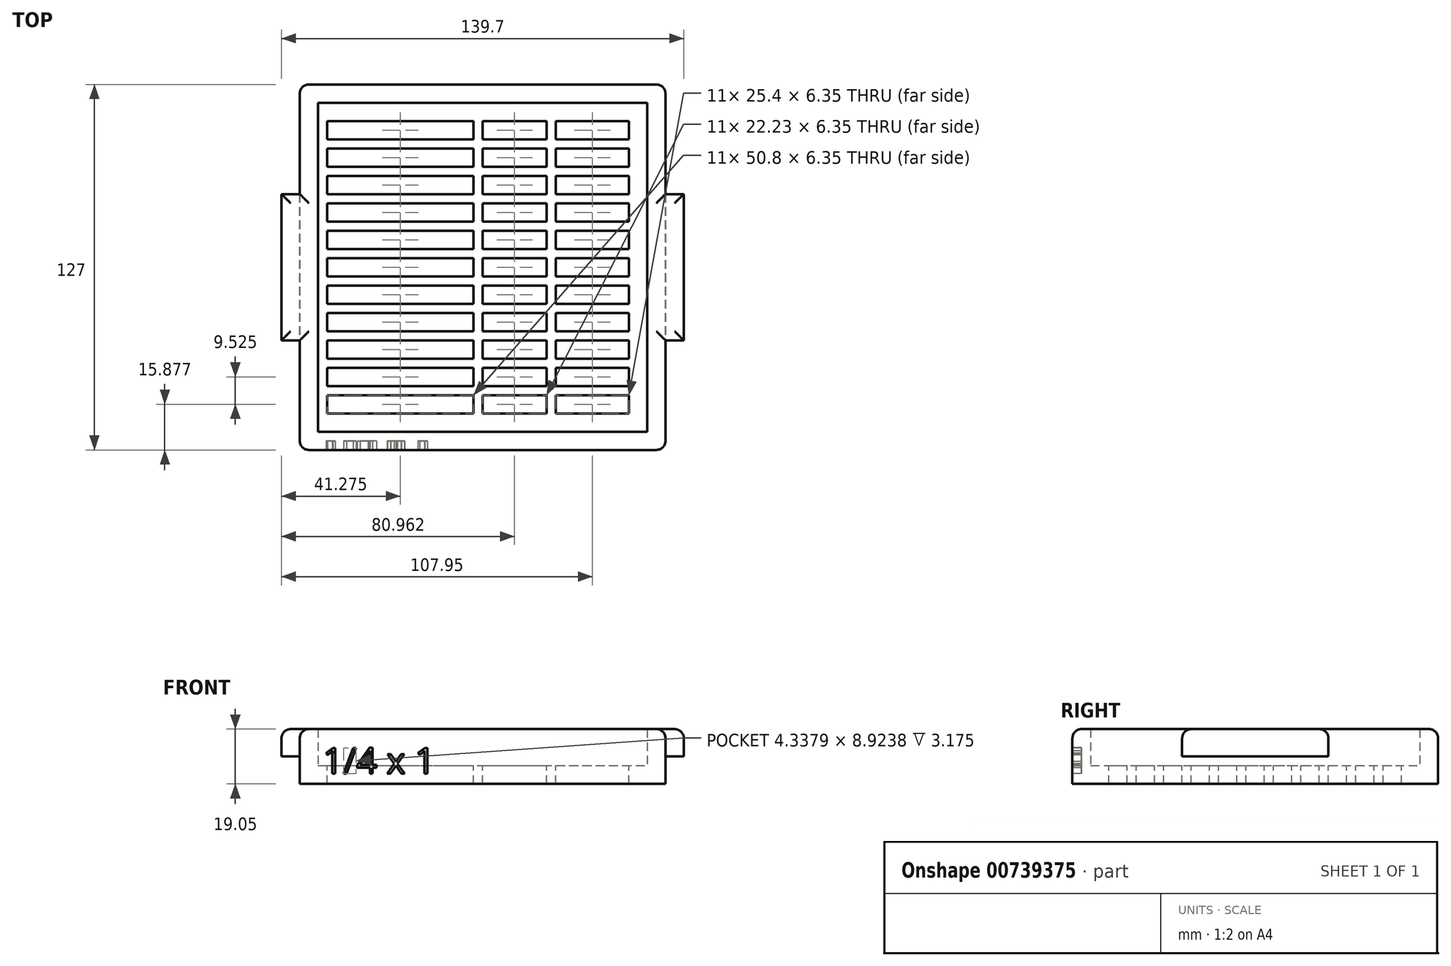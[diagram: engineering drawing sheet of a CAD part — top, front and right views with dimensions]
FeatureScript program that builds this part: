
annotation { "Feature Type Name" : "Feature", "Feature Type Description" : "" }
export const myFeature = defineFeature(function(context is Context, id is Id, definition is map)
    precondition{}
    {
        {
            var Q0;
            Q0=qCreatedBy(makeId("Top.planeOp"),FACE);
            var sketch = newSketch(context, id + "F0", { "sketchPlane" : qUnion([Q0])});
            skLineSegment(sketch, "E0.bottom", {"start": v(-63.5, -63.76) * mm, "end": v(63.5, -63.76) * mm});
            skLineSegment(sketch, "E0.top", {"start": v(-63.5, 63.24) * mm, "end": v(63.5, 63.24) * mm});
            skLineSegment(sketch, "E0.left", {"start": v(-63.5, -63.76) * mm, "end": v(-63.5, 63.24) * mm});
            skLineSegment(sketch, "E0.right", {"start": v(63.5, -63.76) * mm, "end": v(63.5, 63.24) * mm});
            skLineSegment(sketch, "E1.bottom", {"start": v(-57.15, -57.4) * mm, "end": v(57.15, -57.4) * mm});
            skLineSegment(sketch, "E1.top", {"start": v(-57.15, 56.9) * mm, "end": v(57.15, 56.9) * mm});
            skLineSegment(sketch, "E1.left", {"start": v(-57.15, -57.4) * mm, "end": v(-57.15, 56.9) * mm});
            skLineSegment(sketch, "E1.right", {"start": v(57.15, -57.4) * mm, "end": v(57.15, 56.9) * mm});
            skPoint(sketch, "E2", {"position": v(-63.5, -0.26) * mm});
            skPoint(sketch, "E3", {"position": v(63.5, -0.26) * mm});
            skLineSegment(sketch, "E4.bottom", {"start": v(-69.85, 25.14) * mm, "end": v(-57.15, 25.14) * mm});
            skLineSegment(sketch, "E4.top", {"start": v(-69.85, -25.66) * mm, "end": v(-57.15, -25.66) * mm});
            skLineSegment(sketch, "E4.left", {"start": v(-69.85, 25.14) * mm, "end": v(-69.85, -25.66) * mm});
            skLineSegment(sketch, "E4.right", {"start": v(-57.15, 25.14) * mm, "end": v(-57.15, -25.66) * mm});
            skLineSegment(sketch, "E5.bottom", {"start": v(69.85, 25.14) * mm, "end": v(57.15, 25.14) * mm});
            skLineSegment(sketch, "E5.top", {"start": v(69.85, -25.66) * mm, "end": v(57.15, -25.66) * mm});
            skLineSegment(sketch, "E5.left", {"start": v(69.85, 25.14) * mm, "end": v(69.85, -25.66) * mm});
            skLineSegment(sketch, "E5.right", {"start": v(57.15, 25.14) * mm, "end": v(57.15, -25.66) * mm});
            skPoint(sketch, "E5.cornerSnap0", {"position": v(-63.5, 25.14) * mm});
            skSolve(sketch);
        }
        {
            var Q0;
            {var subQ3=sQuery(id+"F0.wireOp",EDGE,"E1.bottom");Q0=makeQuery(id+"F0.imprint","IMPRINT",FACE,{"disambiguationData":[TD([[makeQuery(id+"F0.imprint","IMPRINT",EDGE,{"derivedFrom":subQ3}),1.0]])]});}
            extrude(context, id + "F1", {"entities" : qUnion([Q0]), "depth" : 6.35 * mm, "offsetDistance" : 25.4 * mm});
        }
        {
            var Q0;
            Q0=qSketchRegion(id+"F0",true);
            extrude(context, id + "F2", {"entities" : qUnion([Q0]), "operationType" : NewBodyOperationType.ADD, "depth" : 19.05 * mm, "offsetDistance" : 25.4 * mm});
        }
        {
            var Q0;
            Q0=makeQuery(id+"F1.opExtrude","CAP_FACE",FACE,{"disambiguationData":[OSD([sQuery(id+"F0.wireOp",EDGE,"E1.bottom"),sQuery(id+"F0.wireOp",EDGE,"E1.top"),sQuery(id+"F0.wireOp",EDGE,"E1.left"),sQuery(id+"F0.wireOp",EDGE,"E1.right"),sQuery(id+"F0.wireOp",EDGE,"E4.right"),sQuery(id+"F0.wireOp",EDGE,"E5.right")])],"isStart":false});
            var sketch = newSketch(context, id + "F3", { "sketchPlane" : qUnion([Q0])});
            skLineSegment(sketch, "E6.bottom", {"start": v(-53.97, -51.06) * mm, "end": v(-25.4, -51.06) * mm});
            skLineSegment(sketch, "E6.top", {"start": v(-53.98, -44.7) * mm, "end": v(-25.4, -44.7) * mm});
            skLineSegment(sketch, "E6.left", {"start": v(-53.97, -51.06) * mm, "end": v(-53.97, -44.7) * mm});
            skLineSegment(sketch, "E6.right", {"start": v(-25.4, -51.06) * mm, "end": v(-25.4, -44.7) * mm});
            skLineSegment(sketch, "E7.0.1.0", {"start": v(-53.97, -41.53) * mm, "end": v(-25.4, -41.53) * mm});
            skLineSegment(sketch, "E7.0.1.1", {"start": v(-53.98, -35.18) * mm, "end": v(-25.4, -35.18) * mm});
            skLineSegment(sketch, "E7.0.1.2", {"start": v(-53.97, -41.53) * mm, "end": v(-53.97, -35.18) * mm});
            skLineSegment(sketch, "E7.0.1.3", {"start": v(-25.4, -41.53) * mm, "end": v(-25.4, -35.18) * mm});
            skLineSegment(sketch, "E7.0.2.0", {"start": v(-53.97, -32) * mm, "end": v(-25.4, -32) * mm});
            skLineSegment(sketch, "E7.0.2.1", {"start": v(-53.98, -25.66) * mm, "end": v(-25.4, -25.66) * mm});
            skLineSegment(sketch, "E7.0.2.2", {"start": v(-53.97, -32) * mm, "end": v(-53.97, -25.66) * mm});
            skLineSegment(sketch, "E7.0.2.3", {"start": v(-25.4, -32) * mm, "end": v(-25.4, -25.66) * mm});
            skLineSegment(sketch, "E7.0.3.0", {"start": v(-53.97, -22.48) * mm, "end": v(-25.4, -22.48) * mm});
            skLineSegment(sketch, "E7.0.3.1", {"start": v(-53.98, -16.13) * mm, "end": v(-25.4, -16.13) * mm});
            skLineSegment(sketch, "E7.0.3.2", {"start": v(-53.97, -22.48) * mm, "end": v(-53.97, -16.13) * mm});
            skLineSegment(sketch, "E7.0.3.3", {"start": v(-25.4, -22.48) * mm, "end": v(-25.4, -16.13) * mm});
            skLineSegment(sketch, "E7.0.4.0", {"start": v(-53.97, -12.96) * mm, "end": v(-25.4, -12.96) * mm});
            skLineSegment(sketch, "E7.0.4.1", {"start": v(-53.98, -6.6) * mm, "end": v(-25.4, -6.6) * mm});
            skLineSegment(sketch, "E7.0.4.2", {"start": v(-53.97, -12.96) * mm, "end": v(-53.97, -6.6) * mm});
            skLineSegment(sketch, "E7.0.4.3", {"start": v(-25.4, -12.96) * mm, "end": v(-25.4, -6.6) * mm});
            skLineSegment(sketch, "E7.0.5.0", {"start": v(-53.97, -3.43) * mm, "end": v(-25.4, -3.43) * mm});
            skLineSegment(sketch, "E7.0.5.1", {"start": v(-53.98, 2.92) * mm, "end": v(-25.4, 2.92) * mm});
            skLineSegment(sketch, "E7.0.5.2", {"start": v(-53.97, -3.43) * mm, "end": v(-53.97, 2.92) * mm});
            skLineSegment(sketch, "E7.0.5.3", {"start": v(-25.4, -3.43) * mm, "end": v(-25.4, 2.92) * mm});
            skLineSegment(sketch, "E7.0.6.0", {"start": v(-53.97, 6.1) * mm, "end": v(-25.4, 6.1) * mm});
            skLineSegment(sketch, "E7.0.6.1", {"start": v(-53.98, 12.44) * mm, "end": v(-25.4, 12.44) * mm});
            skLineSegment(sketch, "E7.0.6.2", {"start": v(-53.97, 6.1) * mm, "end": v(-53.97, 12.44) * mm});
            skLineSegment(sketch, "E7.0.6.3", {"start": v(-25.4, 6.1) * mm, "end": v(-25.4, 12.44) * mm});
            skLineSegment(sketch, "E7.0.7.0", {"start": v(-53.97, 15.62) * mm, "end": v(-25.4, 15.62) * mm});
            skLineSegment(sketch, "E7.0.7.1", {"start": v(-53.98, 21.97) * mm, "end": v(-25.4, 21.97) * mm});
            skLineSegment(sketch, "E7.0.7.2", {"start": v(-53.97, 15.62) * mm, "end": v(-53.97, 21.97) * mm});
            skLineSegment(sketch, "E7.0.7.3", {"start": v(-25.4, 15.62) * mm, "end": v(-25.4, 21.97) * mm});
            skLineSegment(sketch, "E7.0.8.0", {"start": v(-53.97, 25.14) * mm, "end": v(-25.4, 25.14) * mm});
            skLineSegment(sketch, "E7.0.8.1", {"start": v(-53.98, 31.5) * mm, "end": v(-25.4, 31.5) * mm});
            skLineSegment(sketch, "E7.0.8.2", {"start": v(-53.97, 25.14) * mm, "end": v(-53.97, 31.5) * mm});
            skLineSegment(sketch, "E7.0.8.3", {"start": v(-25.4, 25.14) * mm, "end": v(-25.4, 31.5) * mm});
            skLineSegment(sketch, "E7.0.9.0", {"start": v(-53.97, 34.67) * mm, "end": v(-25.4, 34.67) * mm});
            skLineSegment(sketch, "E7.0.9.1", {"start": v(-53.98, 41.02) * mm, "end": v(-25.4, 41.02) * mm});
            skLineSegment(sketch, "E7.0.9.2", {"start": v(-53.97, 34.67) * mm, "end": v(-53.97, 41.02) * mm});
            skLineSegment(sketch, "E7.0.9.3", {"start": v(-25.4, 34.67) * mm, "end": v(-25.4, 41.02) * mm});
            skLineSegment(sketch, "E7.0.10.0", {"start": v(-53.97, 44.2) * mm, "end": v(-25.4, 44.2) * mm});
            skLineSegment(sketch, "E7.0.10.1", {"start": v(-53.98, 50.54) * mm, "end": v(-25.4, 50.54) * mm});
            skLineSegment(sketch, "E7.0.10.2", {"start": v(-53.97, 44.2) * mm, "end": v(-53.97, 50.54) * mm});
            skLineSegment(sketch, "E7.0.10.3", {"start": v(-25.4, 44.2) * mm, "end": v(-25.4, 50.54) * mm});
            skLineSegment(sketch, "E7.1.0.0", {"start": v(-28.57, -51.06) * mm, "end": v(0, -51.06) * mm});
            skLineSegment(sketch, "E7.1.0.1", {"start": v(-28.58, -44.7) * mm, "end": v(0, -44.7) * mm});
            skLineSegment(sketch, "E7.1.0.2", {"start": v(-28.57, -51.06) * mm, "end": v(-28.57, -44.7) * mm});
            skLineSegment(sketch, "E7.1.0.3", {"start": v(0, -51.06) * mm, "end": v(0, -44.7) * mm});
            skLineSegment(sketch, "E7.1.1.0", {"start": v(-28.57, -41.53) * mm, "end": v(0, -41.53) * mm});
            skLineSegment(sketch, "E7.1.1.1", {"start": v(-28.58, -35.18) * mm, "end": v(0, -35.18) * mm});
            skLineSegment(sketch, "E7.1.1.2", {"start": v(-28.57, -41.53) * mm, "end": v(-28.58, -35.18) * mm});
            skLineSegment(sketch, "E7.1.1.3", {"start": v(0, -41.53) * mm, "end": v(0, -35.18) * mm});
            skLineSegment(sketch, "E7.1.2.0", {"start": v(-28.57, -32) * mm, "end": v(0, -32) * mm});
            skLineSegment(sketch, "E7.1.2.1", {"start": v(-28.58, -25.66) * mm, "end": v(0, -25.66) * mm});
            skLineSegment(sketch, "E7.1.2.2", {"start": v(-28.57, -32) * mm, "end": v(-28.58, -25.66) * mm});
            skLineSegment(sketch, "E7.1.2.3", {"start": v(0, -32) * mm, "end": v(0, -25.66) * mm});
            skLineSegment(sketch, "E7.1.3.0", {"start": v(-28.57, -22.48) * mm, "end": v(0, -22.48) * mm});
            skLineSegment(sketch, "E7.1.3.1", {"start": v(-28.58, -16.13) * mm, "end": v(0, -16.13) * mm});
            skLineSegment(sketch, "E7.1.3.2", {"start": v(-28.58, -22.48) * mm, "end": v(-28.58, -16.13) * mm});
            skLineSegment(sketch, "E7.1.3.3", {"start": v(0, -22.48) * mm, "end": v(0, -16.13) * mm});
            skLineSegment(sketch, "E7.1.4.0", {"start": v(-28.57, -12.96) * mm, "end": v(0, -12.96) * mm});
            skLineSegment(sketch, "E7.1.4.1", {"start": v(-28.58, -6.6) * mm, "end": v(0, -6.6) * mm});
            skLineSegment(sketch, "E7.1.4.2", {"start": v(-28.58, -12.96) * mm, "end": v(-28.58, -6.6) * mm});
            skLineSegment(sketch, "E7.1.4.3", {"start": v(0, -12.96) * mm, "end": v(0, -6.6) * mm});
            skLineSegment(sketch, "E7.1.5.0", {"start": v(-28.57, -3.43) * mm, "end": v(0, -3.43) * mm});
            skLineSegment(sketch, "E7.1.5.1", {"start": v(-28.58, 2.92) * mm, "end": v(0, 2.92) * mm});
            skLineSegment(sketch, "E7.1.5.2", {"start": v(-28.58, -3.43) * mm, "end": v(-28.58, 2.92) * mm});
            skLineSegment(sketch, "E7.1.5.3", {"start": v(0, -3.43) * mm, "end": v(0, 2.92) * mm});
            skLineSegment(sketch, "E7.1.6.0", {"start": v(-28.57, 6.1) * mm, "end": v(0, 6.1) * mm});
            skLineSegment(sketch, "E7.1.6.1", {"start": v(-28.58, 12.44) * mm, "end": v(0, 12.44) * mm});
            skLineSegment(sketch, "E7.1.6.2", {"start": v(-28.58, 6.1) * mm, "end": v(-28.58, 12.44) * mm});
            skLineSegment(sketch, "E7.1.6.3", {"start": v(0, 6.1) * mm, "end": v(0, 12.44) * mm});
            skLineSegment(sketch, "E7.1.7.0", {"start": v(-28.57, 15.62) * mm, "end": v(0, 15.62) * mm});
            skLineSegment(sketch, "E7.1.7.1", {"start": v(-28.58, 21.97) * mm, "end": v(0, 21.97) * mm});
            skLineSegment(sketch, "E7.1.7.2", {"start": v(-28.58, 15.62) * mm, "end": v(-28.58, 21.97) * mm});
            skLineSegment(sketch, "E7.1.7.3", {"start": v(0, 15.62) * mm, "end": v(0, 21.97) * mm});
            skLineSegment(sketch, "E7.1.8.0", {"start": v(-28.57, 25.14) * mm, "end": v(0, 25.14) * mm});
            skLineSegment(sketch, "E7.1.8.1", {"start": v(-28.58, 31.5) * mm, "end": v(0, 31.5) * mm});
            skLineSegment(sketch, "E7.1.8.2", {"start": v(-28.58, 25.14) * mm, "end": v(-28.58, 31.5) * mm});
            skLineSegment(sketch, "E7.1.8.3", {"start": v(0, 25.14) * mm, "end": v(0, 31.5) * mm});
            skLineSegment(sketch, "E7.1.9.0", {"start": v(-28.57, 34.67) * mm, "end": v(0, 34.67) * mm});
            skLineSegment(sketch, "E7.1.9.1", {"start": v(-28.58, 41.02) * mm, "end": v(0, 41.02) * mm});
            skLineSegment(sketch, "E7.1.9.2", {"start": v(-28.58, 34.67) * mm, "end": v(-28.58, 41.02) * mm});
            skLineSegment(sketch, "E7.1.9.3", {"start": v(0, 34.67) * mm, "end": v(0, 41.02) * mm});
            skLineSegment(sketch, "E7.1.10.0", {"start": v(-28.57, 44.2) * mm, "end": v(0, 44.2) * mm});
            skLineSegment(sketch, "E7.1.10.1", {"start": v(-28.58, 50.54) * mm, "end": v(0, 50.54) * mm});
            skLineSegment(sketch, "E7.1.10.2", {"start": v(-28.58, 44.2) * mm, "end": v(-28.58, 50.54) * mm});
            skLineSegment(sketch, "E7.1.10.3", {"start": v(0, 44.2) * mm, "end": v(0, 50.54) * mm});
            skLineSegment(sketch, "E7.2.0.0", {"start": v(-3.18, -51.06) * mm, "end": v(25.4, -51.06) * mm});
            skLineSegment(sketch, "E7.2.0.1", {"start": v(-3.18, -44.7) * mm, "end": v(25.4, -44.7) * mm});
            skLineSegment(sketch, "E7.2.0.2", {"start": v(-3.18, -51.06) * mm, "end": v(-3.18, -44.7) * mm});
            skLineSegment(sketch, "E7.2.0.3", {"start": v(25.4, -51.06) * mm, "end": v(25.4, -44.7) * mm});
            skLineSegment(sketch, "E7.2.1.0", {"start": v(-3.18, -41.53) * mm, "end": v(25.4, -41.53) * mm});
            skLineSegment(sketch, "E7.2.1.1", {"start": v(-3.18, -35.18) * mm, "end": v(25.4, -35.18) * mm});
            skLineSegment(sketch, "E7.2.1.2", {"start": v(-3.18, -41.53) * mm, "end": v(-3.18, -35.18) * mm});
            skLineSegment(sketch, "E7.2.1.3", {"start": v(25.4, -41.53) * mm, "end": v(25.4, -35.18) * mm});
            skLineSegment(sketch, "E7.2.2.0", {"start": v(-3.18, -32) * mm, "end": v(25.4, -32) * mm});
            skLineSegment(sketch, "E7.2.2.1", {"start": v(-3.18, -25.66) * mm, "end": v(25.4, -25.66) * mm});
            skLineSegment(sketch, "E7.2.2.2", {"start": v(-3.18, -32) * mm, "end": v(-3.18, -25.66) * mm});
            skLineSegment(sketch, "E7.2.2.3", {"start": v(25.4, -32) * mm, "end": v(25.4, -25.66) * mm});
            skLineSegment(sketch, "E7.2.3.0", {"start": v(-3.18, -22.48) * mm, "end": v(25.4, -22.48) * mm});
            skLineSegment(sketch, "E7.2.3.1", {"start": v(-3.18, -16.13) * mm, "end": v(25.4, -16.13) * mm});
            skLineSegment(sketch, "E7.2.3.2", {"start": v(-3.18, -22.48) * mm, "end": v(-3.18, -16.13) * mm});
            skLineSegment(sketch, "E7.2.3.3", {"start": v(25.4, -22.48) * mm, "end": v(25.4, -16.13) * mm});
            skLineSegment(sketch, "E7.2.4.0", {"start": v(-3.18, -12.96) * mm, "end": v(25.4, -12.96) * mm});
            skLineSegment(sketch, "E7.2.4.1", {"start": v(-3.18, -6.6) * mm, "end": v(25.4, -6.6) * mm});
            skLineSegment(sketch, "E7.2.4.2", {"start": v(-3.18, -12.96) * mm, "end": v(-3.18, -6.6) * mm});
            skLineSegment(sketch, "E7.2.4.3", {"start": v(25.4, -12.96) * mm, "end": v(25.4, -6.6) * mm});
            skLineSegment(sketch, "E7.2.5.0", {"start": v(-3.18, -3.43) * mm, "end": v(25.4, -3.43) * mm});
            skLineSegment(sketch, "E7.2.5.1", {"start": v(-3.18, 2.92) * mm, "end": v(25.4, 2.92) * mm});
            skLineSegment(sketch, "E7.2.5.2", {"start": v(-3.18, -3.43) * mm, "end": v(-3.18, 2.92) * mm});
            skLineSegment(sketch, "E7.2.5.3", {"start": v(25.4, -3.43) * mm, "end": v(25.4, 2.92) * mm});
            skLineSegment(sketch, "E7.2.6.0", {"start": v(-3.18, 6.1) * mm, "end": v(25.4, 6.1) * mm});
            skLineSegment(sketch, "E7.2.6.1", {"start": v(-3.18, 12.44) * mm, "end": v(25.4, 12.44) * mm});
            skLineSegment(sketch, "E7.2.6.2", {"start": v(-3.18, 6.1) * mm, "end": v(-3.18, 12.44) * mm});
            skLineSegment(sketch, "E7.2.6.3", {"start": v(25.4, 6.1) * mm, "end": v(25.4, 12.44) * mm});
            skLineSegment(sketch, "E7.2.7.0", {"start": v(-3.18, 15.62) * mm, "end": v(25.4, 15.62) * mm});
            skLineSegment(sketch, "E7.2.7.1", {"start": v(-3.18, 21.97) * mm, "end": v(25.4, 21.97) * mm});
            skLineSegment(sketch, "E7.2.7.2", {"start": v(-3.18, 15.62) * mm, "end": v(-3.18, 21.97) * mm});
            skLineSegment(sketch, "E7.2.7.3", {"start": v(25.4, 15.62) * mm, "end": v(25.4, 21.97) * mm});
            skLineSegment(sketch, "E7.2.8.0", {"start": v(-3.18, 25.14) * mm, "end": v(25.4, 25.14) * mm});
            skLineSegment(sketch, "E7.2.8.1", {"start": v(-3.18, 31.5) * mm, "end": v(25.4, 31.5) * mm});
            skLineSegment(sketch, "E7.2.8.2", {"start": v(-3.18, 25.14) * mm, "end": v(-3.18, 31.5) * mm});
            skLineSegment(sketch, "E7.2.8.3", {"start": v(25.4, 25.14) * mm, "end": v(25.4, 31.5) * mm});
            skLineSegment(sketch, "E7.2.9.0", {"start": v(-3.18, 34.67) * mm, "end": v(25.4, 34.67) * mm});
            skLineSegment(sketch, "E7.2.9.1", {"start": v(-3.18, 41.02) * mm, "end": v(25.4, 41.02) * mm});
            skLineSegment(sketch, "E7.2.9.2", {"start": v(-3.18, 34.67) * mm, "end": v(-3.18, 41.02) * mm});
            skLineSegment(sketch, "E7.2.9.3", {"start": v(25.4, 34.67) * mm, "end": v(25.4, 41.02) * mm});
            skLineSegment(sketch, "E7.2.10.0", {"start": v(-3.18, 44.2) * mm, "end": v(25.4, 44.2) * mm});
            skLineSegment(sketch, "E7.2.10.1", {"start": v(-3.18, 50.54) * mm, "end": v(25.4, 50.54) * mm});
            skLineSegment(sketch, "E7.2.10.2", {"start": v(-3.18, 44.2) * mm, "end": v(-3.18, 50.54) * mm});
            skLineSegment(sketch, "E7.2.10.3", {"start": v(25.4, 44.2) * mm, "end": v(25.4, 50.54) * mm});
            skLineSegment(sketch, "E7.3.0.0", {"start": v(22.22, -51.06) * mm, "end": v(50.8, -51.06) * mm});
            skLineSegment(sketch, "E7.3.0.1", {"start": v(22.22, -44.7) * mm, "end": v(50.8, -44.7) * mm});
            skLineSegment(sketch, "E7.3.0.2", {"start": v(22.22, -51.06) * mm, "end": v(22.22, -44.7) * mm});
            skLineSegment(sketch, "E7.3.0.3", {"start": v(50.8, -51.06) * mm, "end": v(50.8, -44.7) * mm});
            skLineSegment(sketch, "E7.3.1.0", {"start": v(22.22, -41.53) * mm, "end": v(50.8, -41.53) * mm});
            skLineSegment(sketch, "E7.3.1.1", {"start": v(22.22, -35.18) * mm, "end": v(50.8, -35.18) * mm});
            skLineSegment(sketch, "E7.3.1.2", {"start": v(22.22, -41.53) * mm, "end": v(22.22, -35.18) * mm});
            skLineSegment(sketch, "E7.3.1.3", {"start": v(50.8, -41.53) * mm, "end": v(50.8, -35.18) * mm});
            skLineSegment(sketch, "E7.3.2.0", {"start": v(22.22, -32) * mm, "end": v(50.8, -32) * mm});
            skLineSegment(sketch, "E7.3.2.1", {"start": v(22.22, -25.66) * mm, "end": v(50.8, -25.66) * mm});
            skLineSegment(sketch, "E7.3.2.2", {"start": v(22.22, -32) * mm, "end": v(22.22, -25.66) * mm});
            skLineSegment(sketch, "E7.3.2.3", {"start": v(50.8, -32) * mm, "end": v(50.8, -25.66) * mm});
            skLineSegment(sketch, "E7.3.3.0", {"start": v(22.22, -22.48) * mm, "end": v(50.8, -22.48) * mm});
            skLineSegment(sketch, "E7.3.3.1", {"start": v(22.22, -16.13) * mm, "end": v(50.8, -16.13) * mm});
            skLineSegment(sketch, "E7.3.3.2", {"start": v(22.22, -22.48) * mm, "end": v(22.22, -16.13) * mm});
            skLineSegment(sketch, "E7.3.3.3", {"start": v(50.8, -22.48) * mm, "end": v(50.8, -16.13) * mm});
            skLineSegment(sketch, "E7.3.4.0", {"start": v(22.22, -12.96) * mm, "end": v(50.8, -12.96) * mm});
            skLineSegment(sketch, "E7.3.4.1", {"start": v(22.22, -6.6) * mm, "end": v(50.8, -6.6) * mm});
            skLineSegment(sketch, "E7.3.4.2", {"start": v(22.22, -12.96) * mm, "end": v(22.22, -6.6) * mm});
            skLineSegment(sketch, "E7.3.4.3", {"start": v(50.8, -12.96) * mm, "end": v(50.8, -6.6) * mm});
            skLineSegment(sketch, "E7.3.5.0", {"start": v(22.22, -3.43) * mm, "end": v(50.8, -3.43) * mm});
            skLineSegment(sketch, "E7.3.5.1", {"start": v(22.22, 2.92) * mm, "end": v(50.8, 2.92) * mm});
            skLineSegment(sketch, "E7.3.5.2", {"start": v(22.22, -3.43) * mm, "end": v(22.22, 2.92) * mm});
            skLineSegment(sketch, "E7.3.5.3", {"start": v(50.8, -3.43) * mm, "end": v(50.8, 2.92) * mm});
            skLineSegment(sketch, "E7.3.6.0", {"start": v(22.22, 6.1) * mm, "end": v(50.8, 6.1) * mm});
            skLineSegment(sketch, "E7.3.6.1", {"start": v(22.22, 12.44) * mm, "end": v(50.8, 12.44) * mm});
            skLineSegment(sketch, "E7.3.6.2", {"start": v(22.22, 6.1) * mm, "end": v(22.22, 12.44) * mm});
            skLineSegment(sketch, "E7.3.6.3", {"start": v(50.8, 6.1) * mm, "end": v(50.8, 12.44) * mm});
            skLineSegment(sketch, "E7.3.7.0", {"start": v(22.22, 15.62) * mm, "end": v(50.8, 15.62) * mm});
            skLineSegment(sketch, "E7.3.7.1", {"start": v(22.22, 21.97) * mm, "end": v(50.8, 21.97) * mm});
            skLineSegment(sketch, "E7.3.7.2", {"start": v(22.22, 15.62) * mm, "end": v(22.22, 21.97) * mm});
            skLineSegment(sketch, "E7.3.7.3", {"start": v(50.8, 15.62) * mm, "end": v(50.8, 21.97) * mm});
            skLineSegment(sketch, "E7.3.8.0", {"start": v(22.22, 25.14) * mm, "end": v(50.8, 25.14) * mm});
            skLineSegment(sketch, "E7.3.8.1", {"start": v(22.22, 31.5) * mm, "end": v(50.8, 31.5) * mm});
            skLineSegment(sketch, "E7.3.8.2", {"start": v(22.22, 25.14) * mm, "end": v(22.22, 31.5) * mm});
            skLineSegment(sketch, "E7.3.8.3", {"start": v(50.8, 25.14) * mm, "end": v(50.8, 31.5) * mm});
            skLineSegment(sketch, "E7.3.9.0", {"start": v(22.22, 34.67) * mm, "end": v(50.8, 34.67) * mm});
            skLineSegment(sketch, "E7.3.9.1", {"start": v(22.22, 41.02) * mm, "end": v(50.8, 41.02) * mm});
            skLineSegment(sketch, "E7.3.9.2", {"start": v(22.22, 34.67) * mm, "end": v(22.22, 41.02) * mm});
            skLineSegment(sketch, "E7.3.9.3", {"start": v(50.8, 34.67) * mm, "end": v(50.8, 41.02) * mm});
            skLineSegment(sketch, "E7.3.10.0", {"start": v(22.22, 44.2) * mm, "end": v(50.8, 44.2) * mm});
            skLineSegment(sketch, "E7.3.10.1", {"start": v(22.22, 50.54) * mm, "end": v(50.8, 50.54) * mm});
            skLineSegment(sketch, "E7.3.10.2", {"start": v(22.22, 44.2) * mm, "end": v(22.22, 50.54) * mm});
            skLineSegment(sketch, "E7.3.10.3", {"start": v(50.8, 44.2) * mm, "end": v(50.8, 50.54) * mm});
            skLineSegment(sketch, "E7.direction1", {"start": v(-53.97, -51.06) * mm, "end": v(-28.57, -51.06) * mm, "construction": true});
            skLineSegment(sketch, "E7.direction2", {"start": v(-53.97, -51.06) * mm, "end": v(-53.97, -41.53) * mm, "construction": true});
            skSolve(sketch);
        }
        {
            var Q0;
            Q0=makeQuery(id+"F3.imprint","IMPRINT",FACE,{"disambiguationData":[TD([[makeQuery(id+"F3.imprint","IMPRINT",EDGE,{"derivedFrom":sQuery(id+"F3.wireOp",EDGE,"E6.bottom")}),1.0]])]});
            var Q1;
            Q1=makeQuery(id+"F3.imprint","IMPRINT",FACE,{"disambiguationData":[TD([[makeQuery(id+"F3.imprint","IMPRINT",EDGE,{"derivedFrom":sQuery(id+"F3.wireOp",EDGE,"E7.0.1.0")}),1.0]])]});
            var Q2;
            Q2=makeQuery(id+"F3.imprint","IMPRINT",FACE,{"disambiguationData":[TD([[makeQuery(id+"F3.imprint","IMPRINT",EDGE,{"derivedFrom":sQuery(id+"F3.wireOp",EDGE,"E7.0.2.0")}),1.0]])]});
            var Q3;
            Q3=makeQuery(id+"F3.imprint","IMPRINT",FACE,{"disambiguationData":[TD([[makeQuery(id+"F3.imprint","IMPRINT",EDGE,{"derivedFrom":sQuery(id+"F3.wireOp",EDGE,"E7.0.3.0")}),1.0]])]});
            var Q4;
            Q4=makeQuery(id+"F3.imprint","IMPRINT",FACE,{"disambiguationData":[TD([[makeQuery(id+"F3.imprint","IMPRINT",EDGE,{"derivedFrom":sQuery(id+"F3.wireOp",EDGE,"E7.0.4.0")}),1.0]])]});
            var Q5;
            Q5=makeQuery(id+"F3.imprint","IMPRINT",FACE,{"disambiguationData":[TD([[makeQuery(id+"F3.imprint","IMPRINT",EDGE,{"derivedFrom":sQuery(id+"F3.wireOp",EDGE,"E7.0.5.0")}),1.0]])]});
            var Q6;
            Q6=makeQuery(id+"F3.imprint","IMPRINT",FACE,{"disambiguationData":[TD([[makeQuery(id+"F3.imprint","IMPRINT",EDGE,{"derivedFrom":sQuery(id+"F3.wireOp",EDGE,"E7.0.6.0")}),1.0]])]});
            var Q7;
            Q7=makeQuery(id+"F3.imprint","IMPRINT",FACE,{"disambiguationData":[TD([[makeQuery(id+"F3.imprint","IMPRINT",EDGE,{"derivedFrom":sQuery(id+"F3.wireOp",EDGE,"E7.0.7.0")}),1.0]])]});
            var Q8;
            Q8=makeQuery(id+"F3.imprint","IMPRINT",FACE,{"disambiguationData":[TD([[makeQuery(id+"F3.imprint","IMPRINT",EDGE,{"derivedFrom":sQuery(id+"F3.wireOp",EDGE,"E7.0.8.0")}),1.0]])]});
            var Q9;
            Q9=makeQuery(id+"F3.imprint","IMPRINT",FACE,{"disambiguationData":[TD([[makeQuery(id+"F3.imprint","IMPRINT",EDGE,{"derivedFrom":sQuery(id+"F3.wireOp",EDGE,"E7.0.9.0")}),1.0]])]});
            var Q10;
            Q10=makeQuery(id+"F3.imprint","IMPRINT",FACE,{"disambiguationData":[TD([[makeQuery(id+"F3.imprint","IMPRINT",EDGE,{"derivedFrom":sQuery(id+"F3.wireOp",EDGE,"E7.0.10.0")}),1.0]])]});
            var Q11;
            Q11=makeQuery(id+"F3.imprint","IMPRINT",FACE,{"disambiguationData":[TD([[makeQuery(id+"F3.imprint","IMPRINT",EDGE,{"derivedFrom":sQuery(id+"F3.wireOp",EDGE,"E7.0.11.0")}),1.0]])]});
            var Q12;
            Q12=makeQuery(id+"F3.imprint","IMPRINT",FACE,{"disambiguationData":[TD([[makeQuery(id+"F3.imprint","IMPRINT",EDGE,{"derivedFrom":sQuery(id+"F3.wireOp",EDGE,"E7.0.12.0")}),1.0]])]});
            var Q13;
            Q13=makeQuery(id+"F3.imprint","IMPRINT",FACE,{"disambiguationData":[TD([[makeQuery(id+"F3.imprint","IMPRINT",EDGE,{"derivedFrom":sQuery(id+"F3.wireOp",EDGE,"E7.0.13.0")}),1.0]])]});
            var Q14;
            Q14=makeQuery(id+"F3.imprint","IMPRINT",FACE,{"disambiguationData":[TD([[makeQuery(id+"F3.imprint","IMPRINT",EDGE,{"derivedFrom":sQuery(id+"F3.wireOp",EDGE,"E7.0.14.0")}),1.0]])]});
            var Q15;
            Q15=makeQuery(id+"F3.imprint","IMPRINT",FACE,{"disambiguationData":[TD([[makeQuery(id+"F3.imprint","IMPRINT",EDGE,{"derivedFrom":sQuery(id+"F3.wireOp",EDGE,"E7.0.15.0")}),1.0]])]});
            var Q16;
            Q16=makeQuery(id+"F3.imprint","IMPRINT",FACE,{"disambiguationData":[TD([[makeQuery(id+"F3.imprint","IMPRINT",EDGE,{"derivedFrom":sQuery(id+"F3.wireOp",EDGE,"E7.0.16.0")}),1.0]])]});
            var Q17;
            Q17=makeQuery(id+"F3.imprint","IMPRINT",FACE,{"disambiguationData":[TD([[makeQuery(id+"F3.imprint","IMPRINT",EDGE,{"derivedFrom":sQuery(id+"F3.wireOp",EDGE,"E7.0.17.0")}),1.0]])]});
            var Q18;
            Q18=makeQuery(id+"F3.imprint","IMPRINT",FACE,{"disambiguationData":[TD([[makeQuery(id+"F3.imprint","IMPRINT",EDGE,{"derivedFrom":sQuery(id+"F3.wireOp",EDGE,"E7.0.18.0")}),1.0]])]});
            var Q19;
            Q19=makeQuery(id+"F3.imprint","IMPRINT",FACE,{"disambiguationData":[TD([[makeQuery(id+"F3.imprint","IMPRINT",EDGE,{"derivedFrom":sQuery(id+"F3.wireOp",EDGE,"E7.0.19.0")}),1.0]])]});
            var Q20;
            Q20=makeQuery(id+"F3.imprint","IMPRINT",FACE,{"disambiguationData":[TD([[makeQuery(id+"F3.imprint","IMPRINT",EDGE,{"derivedFrom":sQuery(id+"F3.wireOp",EDGE,"E7.0.20.0")}),1.0]])]});
            var Q21;
            Q21=makeQuery(id+"F3.imprint","IMPRINT",FACE,{"disambiguationData":[TD([[makeQuery(id+"F3.imprint","IMPRINT",EDGE,{"derivedFrom":sQuery(id+"F3.wireOp",EDGE,"E7.0.21.0")}),1.0]])]});
            var Q22;
            {var subQ0=sQuery(id+"F3.wireOp",EDGE,"E6.right");Q22=makeQuery(id+"F3.imprint","IMPRINT",FACE,{"disambiguationData":[TD([[makeQuery(id+"F3.imprint","IMPRINT",EDGE,{"derivedFrom":subQ0}),-1.0]])]});}
            var Q23;
            {var subQ0=sQuery(id+"F3.wireOp",EDGE,"E7.0.1.3");Q23=makeQuery(id+"F3.imprint","IMPRINT",FACE,{"disambiguationData":[TD([[makeQuery(id+"F3.imprint","IMPRINT",EDGE,{"derivedFrom":subQ0}),-1.0]])]});}
            var Q24;
            {var subQ0=sQuery(id+"F3.wireOp",EDGE,"E7.1.0.3");Q24=makeQuery(id+"F3.imprint","IMPRINT",FACE,{"disambiguationData":[TD([[makeQuery(id+"F3.imprint","IMPRINT",EDGE,{"derivedFrom":subQ0}),-1.0]])]});}
            var Q25;
            {var subQ0=sQuery(id+"F3.wireOp",EDGE,"E7.1.1.3");Q25=makeQuery(id+"F3.imprint","IMPRINT",FACE,{"disambiguationData":[TD([[makeQuery(id+"F3.imprint","IMPRINT",EDGE,{"derivedFrom":subQ0}),-1.0]])]});}
            var Q26;
            {var subQ0=sQuery(id+"F3.wireOp",EDGE,"E7.2.0.3");Q26=makeQuery(id+"F3.imprint","IMPRINT",FACE,{"disambiguationData":[TD([[makeQuery(id+"F3.imprint","IMPRINT",EDGE,{"derivedFrom":subQ0}),-1.0]])]});}
            var Q27;
            {var subQ0=sQuery(id+"F3.wireOp",EDGE,"E7.2.1.3");Q27=makeQuery(id+"F3.imprint","IMPRINT",FACE,{"disambiguationData":[TD([[makeQuery(id+"F3.imprint","IMPRINT",EDGE,{"derivedFrom":subQ0}),-1.0]])]});}
            var Q28;
            {var subQ0=sQuery(id+"F3.wireOp",EDGE,"E7.2.2.3");Q28=makeQuery(id+"F3.imprint","IMPRINT",FACE,{"disambiguationData":[TD([[makeQuery(id+"F3.imprint","IMPRINT",EDGE,{"derivedFrom":subQ0}),-1.0]])]});}
            var Q29;
            {var subQ0=sQuery(id+"F3.wireOp",EDGE,"E7.2.3.3");Q29=makeQuery(id+"F3.imprint","IMPRINT",FACE,{"disambiguationData":[TD([[makeQuery(id+"F3.imprint","IMPRINT",EDGE,{"derivedFrom":subQ0}),-1.0]])]});}
            var Q30;
            {var subQ0=sQuery(id+"F3.wireOp",EDGE,"E7.1.3.3");Q30=makeQuery(id+"F3.imprint","IMPRINT",FACE,{"disambiguationData":[TD([[makeQuery(id+"F3.imprint","IMPRINT",EDGE,{"derivedFrom":subQ0}),-1.0]])]});}
            var Q31;
            {var subQ0=sQuery(id+"F3.wireOp",EDGE,"E7.1.2.3");Q31=makeQuery(id+"F3.imprint","IMPRINT",FACE,{"disambiguationData":[TD([[makeQuery(id+"F3.imprint","IMPRINT",EDGE,{"derivedFrom":subQ0}),-1.0]])]});}
            var Q32;
            {var subQ0=sQuery(id+"F3.wireOp",EDGE,"E7.0.2.3");Q32=makeQuery(id+"F3.imprint","IMPRINT",FACE,{"disambiguationData":[TD([[makeQuery(id+"F3.imprint","IMPRINT",EDGE,{"derivedFrom":subQ0}),-1.0]])]});}
            var Q33;
            {var subQ0=sQuery(id+"F3.wireOp",EDGE,"E7.0.3.3");Q33=makeQuery(id+"F3.imprint","IMPRINT",FACE,{"disambiguationData":[TD([[makeQuery(id+"F3.imprint","IMPRINT",EDGE,{"derivedFrom":subQ0}),-1.0]])]});}
            var Q34;
            {var subQ0=sQuery(id+"F3.wireOp",EDGE,"E7.2.4.3");Q34=makeQuery(id+"F3.imprint","IMPRINT",FACE,{"disambiguationData":[TD([[makeQuery(id+"F3.imprint","IMPRINT",EDGE,{"derivedFrom":subQ0}),-1.0]])]});}
            var Q35;
            {var subQ0=sQuery(id+"F3.wireOp",EDGE,"E7.2.5.3");Q35=makeQuery(id+"F3.imprint","IMPRINT",FACE,{"disambiguationData":[TD([[makeQuery(id+"F3.imprint","IMPRINT",EDGE,{"derivedFrom":subQ0}),-1.0]])]});}
            var Q36;
            {var subQ0=sQuery(id+"F3.wireOp",EDGE,"E7.2.6.3");Q36=makeQuery(id+"F3.imprint","IMPRINT",FACE,{"disambiguationData":[TD([[makeQuery(id+"F3.imprint","IMPRINT",EDGE,{"derivedFrom":subQ0}),-1.0]])]});}
            var Q37;
            {var subQ0=sQuery(id+"F3.wireOp",EDGE,"E7.1.4.3");Q37=makeQuery(id+"F3.imprint","IMPRINT",FACE,{"disambiguationData":[TD([[makeQuery(id+"F3.imprint","IMPRINT",EDGE,{"derivedFrom":subQ0}),-1.0]])]});}
            var Q38;
            {var subQ0=sQuery(id+"F3.wireOp",EDGE,"E7.1.5.3");Q38=makeQuery(id+"F3.imprint","IMPRINT",FACE,{"disambiguationData":[TD([[makeQuery(id+"F3.imprint","IMPRINT",EDGE,{"derivedFrom":subQ0}),-1.0]])]});}
            var Q39;
            {var subQ0=sQuery(id+"F3.wireOp",EDGE,"E7.1.6.3");Q39=makeQuery(id+"F3.imprint","IMPRINT",FACE,{"disambiguationData":[TD([[makeQuery(id+"F3.imprint","IMPRINT",EDGE,{"derivedFrom":subQ0}),-1.0]])]});}
            var Q40;
            {var subQ0=sQuery(id+"F3.wireOp",EDGE,"E7.0.4.3");Q40=makeQuery(id+"F3.imprint","IMPRINT",FACE,{"disambiguationData":[TD([[makeQuery(id+"F3.imprint","IMPRINT",EDGE,{"derivedFrom":subQ0}),-1.0]])]});}
            var Q41;
            {var subQ0=sQuery(id+"F3.wireOp",EDGE,"E7.0.5.3");Q41=makeQuery(id+"F3.imprint","IMPRINT",FACE,{"disambiguationData":[TD([[makeQuery(id+"F3.imprint","IMPRINT",EDGE,{"derivedFrom":subQ0}),-1.0]])]});}
            var Q42;
            {var subQ0=sQuery(id+"F3.wireOp",EDGE,"E7.0.6.3");Q42=makeQuery(id+"F3.imprint","IMPRINT",FACE,{"disambiguationData":[TD([[makeQuery(id+"F3.imprint","IMPRINT",EDGE,{"derivedFrom":subQ0}),-1.0]])]});}
            var Q43;
            {var subQ0=sQuery(id+"F3.wireOp",EDGE,"E7.0.7.3");Q43=makeQuery(id+"F3.imprint","IMPRINT",FACE,{"disambiguationData":[TD([[makeQuery(id+"F3.imprint","IMPRINT",EDGE,{"derivedFrom":subQ0}),-1.0]])]});}
            var Q44;
            {var subQ0=sQuery(id+"F3.wireOp",EDGE,"E7.0.8.3");Q44=makeQuery(id+"F3.imprint","IMPRINT",FACE,{"disambiguationData":[TD([[makeQuery(id+"F3.imprint","IMPRINT",EDGE,{"derivedFrom":subQ0}),-1.0]])]});}
            var Q45;
            {var subQ0=sQuery(id+"F3.wireOp",EDGE,"E7.0.9.3");Q45=makeQuery(id+"F3.imprint","IMPRINT",FACE,{"disambiguationData":[TD([[makeQuery(id+"F3.imprint","IMPRINT",EDGE,{"derivedFrom":subQ0}),-1.0]])]});}
            var Q46;
            {var subQ0=sQuery(id+"F3.wireOp",EDGE,"E7.0.10.3");Q46=makeQuery(id+"F3.imprint","IMPRINT",FACE,{"disambiguationData":[TD([[makeQuery(id+"F3.imprint","IMPRINT",EDGE,{"derivedFrom":subQ0}),-1.0]])]});}
            var Q47;
            {var subQ0=sQuery(id+"F3.wireOp",EDGE,"E7.1.7.3");Q47=makeQuery(id+"F3.imprint","IMPRINT",FACE,{"disambiguationData":[TD([[makeQuery(id+"F3.imprint","IMPRINT",EDGE,{"derivedFrom":subQ0}),-1.0]])]});}
            var Q48;
            {var subQ0=sQuery(id+"F3.wireOp",EDGE,"E7.1.8.3");Q48=makeQuery(id+"F3.imprint","IMPRINT",FACE,{"disambiguationData":[TD([[makeQuery(id+"F3.imprint","IMPRINT",EDGE,{"derivedFrom":subQ0}),-1.0]])]});}
            var Q49;
            {var subQ0=sQuery(id+"F3.wireOp",EDGE,"E7.1.9.3");Q49=makeQuery(id+"F3.imprint","IMPRINT",FACE,{"disambiguationData":[TD([[makeQuery(id+"F3.imprint","IMPRINT",EDGE,{"derivedFrom":subQ0}),-1.0]])]});}
            var Q50;
            {var subQ0=sQuery(id+"F3.wireOp",EDGE,"E7.1.10.3");Q50=makeQuery(id+"F3.imprint","IMPRINT",FACE,{"disambiguationData":[TD([[makeQuery(id+"F3.imprint","IMPRINT",EDGE,{"derivedFrom":subQ0}),-1.0]])]});}
            var Q51;
            {var subQ0=sQuery(id+"F3.wireOp",EDGE,"E7.2.10.3");Q51=makeQuery(id+"F3.imprint","IMPRINT",FACE,{"disambiguationData":[TD([[makeQuery(id+"F3.imprint","IMPRINT",EDGE,{"derivedFrom":subQ0}),-1.0]])]});}
            var Q52;
            {var subQ0=sQuery(id+"F3.wireOp",EDGE,"E7.2.9.3");Q52=makeQuery(id+"F3.imprint","IMPRINT",FACE,{"disambiguationData":[TD([[makeQuery(id+"F3.imprint","IMPRINT",EDGE,{"derivedFrom":subQ0}),-1.0]])]});}
            var Q53;
            {var subQ0=sQuery(id+"F3.wireOp",EDGE,"E7.2.8.3");Q53=makeQuery(id+"F3.imprint","IMPRINT",FACE,{"disambiguationData":[TD([[makeQuery(id+"F3.imprint","IMPRINT",EDGE,{"derivedFrom":subQ0}),-1.0]])]});}
            var Q54;
            {var subQ0=sQuery(id+"F3.wireOp",EDGE,"E7.2.7.3");Q54=makeQuery(id+"F3.imprint","IMPRINT",FACE,{"disambiguationData":[TD([[makeQuery(id+"F3.imprint","IMPRINT",EDGE,{"derivedFrom":subQ0}),-1.0]])]});}
            var Q55;
            {var subQ0=sQuery(id+"F3.wireOp",EDGE,"E7.0.11.3");Q55=makeQuery(id+"F3.imprint","IMPRINT",FACE,{"disambiguationData":[TD([[makeQuery(id+"F3.imprint","IMPRINT",EDGE,{"derivedFrom":subQ0}),-1.0]])]});}
            var Q56;
            {var subQ0=sQuery(id+"F3.wireOp",EDGE,"E7.0.12.3");Q56=makeQuery(id+"F3.imprint","IMPRINT",FACE,{"disambiguationData":[TD([[makeQuery(id+"F3.imprint","IMPRINT",EDGE,{"derivedFrom":subQ0}),-1.0]])]});}
            var Q57;
            {var subQ0=sQuery(id+"F3.wireOp",EDGE,"E7.0.13.3");Q57=makeQuery(id+"F3.imprint","IMPRINT",FACE,{"disambiguationData":[TD([[makeQuery(id+"F3.imprint","IMPRINT",EDGE,{"derivedFrom":subQ0}),-1.0]])]});}
            var Q58;
            {var subQ0=sQuery(id+"F3.wireOp",EDGE,"E7.0.14.3");Q58=makeQuery(id+"F3.imprint","IMPRINT",FACE,{"disambiguationData":[TD([[makeQuery(id+"F3.imprint","IMPRINT",EDGE,{"derivedFrom":subQ0}),-1.0]])]});}
            var Q59;
            {var subQ0=sQuery(id+"F3.wireOp",EDGE,"E7.0.15.3");Q59=makeQuery(id+"F3.imprint","IMPRINT",FACE,{"disambiguationData":[TD([[makeQuery(id+"F3.imprint","IMPRINT",EDGE,{"derivedFrom":subQ0}),-1.0]])]});}
            var Q60;
            {var subQ0=sQuery(id+"F3.wireOp",EDGE,"E7.0.16.3");Q60=makeQuery(id+"F3.imprint","IMPRINT",FACE,{"disambiguationData":[TD([[makeQuery(id+"F3.imprint","IMPRINT",EDGE,{"derivedFrom":subQ0}),-1.0]])]});}
            var Q61;
            {var subQ0=sQuery(id+"F3.wireOp",EDGE,"E7.0.17.3");Q61=makeQuery(id+"F3.imprint","IMPRINT",FACE,{"disambiguationData":[TD([[makeQuery(id+"F3.imprint","IMPRINT",EDGE,{"derivedFrom":subQ0}),-1.0]])]});}
            var Q62;
            {var subQ0=sQuery(id+"F3.wireOp",EDGE,"E7.0.18.3");Q62=makeQuery(id+"F3.imprint","IMPRINT",FACE,{"disambiguationData":[TD([[makeQuery(id+"F3.imprint","IMPRINT",EDGE,{"derivedFrom":subQ0}),-1.0]])]});}
            var Q63;
            {var subQ0=sQuery(id+"F3.wireOp",EDGE,"E7.0.19.3");Q63=makeQuery(id+"F3.imprint","IMPRINT",FACE,{"disambiguationData":[TD([[makeQuery(id+"F3.imprint","IMPRINT",EDGE,{"derivedFrom":subQ0}),-1.0]])]});}
            var Q64;
            {var subQ0=sQuery(id+"F3.wireOp",EDGE,"E7.0.20.3");Q64=makeQuery(id+"F3.imprint","IMPRINT",FACE,{"disambiguationData":[TD([[makeQuery(id+"F3.imprint","IMPRINT",EDGE,{"derivedFrom":subQ0}),-1.0]])]});}
            var Q65;
            {var subQ0=sQuery(id+"F3.wireOp",EDGE,"E7.0.21.3");Q65=makeQuery(id+"F3.imprint","IMPRINT",FACE,{"disambiguationData":[TD([[makeQuery(id+"F3.imprint","IMPRINT",EDGE,{"derivedFrom":subQ0}),-1.0]])]});}
            var Q66;
            {var subQ0=sQuery(id+"F3.wireOp",EDGE,"E7.1.21.3");Q66=makeQuery(id+"F3.imprint","IMPRINT",FACE,{"disambiguationData":[TD([[makeQuery(id+"F3.imprint","IMPRINT",EDGE,{"derivedFrom":subQ0}),-1.0]])]});}
            var Q67;
            {var subQ0=sQuery(id+"F3.wireOp",EDGE,"E7.1.20.3");Q67=makeQuery(id+"F3.imprint","IMPRINT",FACE,{"disambiguationData":[TD([[makeQuery(id+"F3.imprint","IMPRINT",EDGE,{"derivedFrom":subQ0}),-1.0]])]});}
            var Q68;
            {var subQ0=sQuery(id+"F3.wireOp",EDGE,"E7.1.19.3");Q68=makeQuery(id+"F3.imprint","IMPRINT",FACE,{"disambiguationData":[TD([[makeQuery(id+"F3.imprint","IMPRINT",EDGE,{"derivedFrom":subQ0}),-1.0]])]});}
            var Q69;
            {var subQ0=sQuery(id+"F3.wireOp",EDGE,"E7.1.18.3");Q69=makeQuery(id+"F3.imprint","IMPRINT",FACE,{"disambiguationData":[TD([[makeQuery(id+"F3.imprint","IMPRINT",EDGE,{"derivedFrom":subQ0}),-1.0]])]});}
            var Q70;
            {var subQ0=sQuery(id+"F3.wireOp",EDGE,"E7.1.17.3");Q70=makeQuery(id+"F3.imprint","IMPRINT",FACE,{"disambiguationData":[TD([[makeQuery(id+"F3.imprint","IMPRINT",EDGE,{"derivedFrom":subQ0}),-1.0]])]});}
            var Q71;
            {var subQ0=sQuery(id+"F3.wireOp",EDGE,"E7.1.16.3");Q71=makeQuery(id+"F3.imprint","IMPRINT",FACE,{"disambiguationData":[TD([[makeQuery(id+"F3.imprint","IMPRINT",EDGE,{"derivedFrom":subQ0}),-1.0]])]});}
            var Q72;
            {var subQ0=sQuery(id+"F3.wireOp",EDGE,"E7.1.15.3");Q72=makeQuery(id+"F3.imprint","IMPRINT",FACE,{"disambiguationData":[TD([[makeQuery(id+"F3.imprint","IMPRINT",EDGE,{"derivedFrom":subQ0}),-1.0]])]});}
            var Q73;
            {var subQ0=sQuery(id+"F3.wireOp",EDGE,"E7.1.14.3");Q73=makeQuery(id+"F3.imprint","IMPRINT",FACE,{"disambiguationData":[TD([[makeQuery(id+"F3.imprint","IMPRINT",EDGE,{"derivedFrom":subQ0}),-1.0]])]});}
            var Q74;
            {var subQ0=sQuery(id+"F3.wireOp",EDGE,"E7.1.13.3");Q74=makeQuery(id+"F3.imprint","IMPRINT",FACE,{"disambiguationData":[TD([[makeQuery(id+"F3.imprint","IMPRINT",EDGE,{"derivedFrom":subQ0}),-1.0]])]});}
            var Q75;
            {var subQ0=sQuery(id+"F3.wireOp",EDGE,"E7.1.12.3");Q75=makeQuery(id+"F3.imprint","IMPRINT",FACE,{"disambiguationData":[TD([[makeQuery(id+"F3.imprint","IMPRINT",EDGE,{"derivedFrom":subQ0}),-1.0]])]});}
            var Q76;
            {var subQ0=sQuery(id+"F3.wireOp",EDGE,"E7.1.11.3");Q76=makeQuery(id+"F3.imprint","IMPRINT",FACE,{"disambiguationData":[TD([[makeQuery(id+"F3.imprint","IMPRINT",EDGE,{"derivedFrom":subQ0}),-1.0]])]});}
            var Q77;
            {var subQ0=sQuery(id+"F3.wireOp",EDGE,"E7.2.11.3");Q77=makeQuery(id+"F3.imprint","IMPRINT",FACE,{"disambiguationData":[TD([[makeQuery(id+"F3.imprint","IMPRINT",EDGE,{"derivedFrom":subQ0}),-1.0]])]});}
            var Q78;
            {var subQ0=sQuery(id+"F3.wireOp",EDGE,"E7.2.12.3");Q78=makeQuery(id+"F3.imprint","IMPRINT",FACE,{"disambiguationData":[TD([[makeQuery(id+"F3.imprint","IMPRINT",EDGE,{"derivedFrom":subQ0}),-1.0]])]});}
            var Q79;
            {var subQ0=sQuery(id+"F3.wireOp",EDGE,"E7.2.13.3");Q79=makeQuery(id+"F3.imprint","IMPRINT",FACE,{"disambiguationData":[TD([[makeQuery(id+"F3.imprint","IMPRINT",EDGE,{"derivedFrom":subQ0}),-1.0]])]});}
            var Q80;
            {var subQ0=sQuery(id+"F3.wireOp",EDGE,"E7.2.14.3");Q80=makeQuery(id+"F3.imprint","IMPRINT",FACE,{"disambiguationData":[TD([[makeQuery(id+"F3.imprint","IMPRINT",EDGE,{"derivedFrom":subQ0}),-1.0]])]});}
            var Q81;
            {var subQ0=sQuery(id+"F3.wireOp",EDGE,"E7.2.15.3");Q81=makeQuery(id+"F3.imprint","IMPRINT",FACE,{"disambiguationData":[TD([[makeQuery(id+"F3.imprint","IMPRINT",EDGE,{"derivedFrom":subQ0}),-1.0]])]});}
            var Q82;
            {var subQ0=sQuery(id+"F3.wireOp",EDGE,"E7.2.16.3");Q82=makeQuery(id+"F3.imprint","IMPRINT",FACE,{"disambiguationData":[TD([[makeQuery(id+"F3.imprint","IMPRINT",EDGE,{"derivedFrom":subQ0}),-1.0]])]});}
            var Q83;
            {var subQ0=sQuery(id+"F3.wireOp",EDGE,"E7.2.17.3");Q83=makeQuery(id+"F3.imprint","IMPRINT",FACE,{"disambiguationData":[TD([[makeQuery(id+"F3.imprint","IMPRINT",EDGE,{"derivedFrom":subQ0}),-1.0]])]});}
            var Q84;
            {var subQ0=sQuery(id+"F3.wireOp",EDGE,"E7.2.18.3");Q84=makeQuery(id+"F3.imprint","IMPRINT",FACE,{"disambiguationData":[TD([[makeQuery(id+"F3.imprint","IMPRINT",EDGE,{"derivedFrom":subQ0}),-1.0]])]});}
            var Q85;
            {var subQ0=sQuery(id+"F3.wireOp",EDGE,"E7.2.19.3");Q85=makeQuery(id+"F3.imprint","IMPRINT",FACE,{"disambiguationData":[TD([[makeQuery(id+"F3.imprint","IMPRINT",EDGE,{"derivedFrom":subQ0}),-1.0]])]});}
            var Q86;
            {var subQ0=sQuery(id+"F3.wireOp",EDGE,"E7.2.20.3");Q86=makeQuery(id+"F3.imprint","IMPRINT",FACE,{"disambiguationData":[TD([[makeQuery(id+"F3.imprint","IMPRINT",EDGE,{"derivedFrom":subQ0}),-1.0]])]});}
            var Q87;
            {var subQ0=sQuery(id+"F3.wireOp",EDGE,"E7.2.21.3");Q87=makeQuery(id+"F3.imprint","IMPRINT",FACE,{"disambiguationData":[TD([[makeQuery(id+"F3.imprint","IMPRINT",EDGE,{"derivedFrom":subQ0}),-1.0]])]});}
            extrude(context, id + "F4", {"entities" : qUnion([Q0, Q1, Q2, Q3, Q4, Q5, Q6, Q7, Q8, Q9, Q10, Q11, Q12, Q13, Q14, Q15, Q16, Q17, Q18, Q19, Q20, Q21, Q22, Q23, Q24, Q25, Q26, Q27, Q28, Q29, Q30, Q31, Q32, Q33, Q34, Q35, Q36, Q37, Q38, Q39, Q40, Q41, Q42, Q43, Q44, Q45, Q46, Q47, Q48, Q49, Q50, Q51, Q52, Q53, Q54, Q55, Q56, Q57, Q58, Q59, Q60, Q61, Q62, Q63, Q64, Q65, Q66, Q67, Q68, Q69, Q70, Q71, Q72, Q73, Q74, Q75, Q76, Q77, Q78, Q79, Q80, Q81, Q82, Q83, Q84, Q85, Q86, Q87]), "operationType" : NewBodyOperationType.REMOVE, "oppositeDirection" : true, "depth" : 25.4 * mm, "offsetDistance" : 25.4 * mm});
        }
        {
            var Q0;
            {var subQ0=sQuery(id+"F0.wireOp",EDGE,"E0.left");Q0=makeQuery(id+"F2.opExtrude","CAP_EDGE",EDGE,{"disambiguationData":[OSD([subQ0]),TDD([makeQuery(id+"F0.imprint","IMPRINT",EDGE,{"disambiguationData":[TD([[makeQuery(id+"F0.imprint","INTERSECT",VERTEX,{"derivedFrom":[sQuery(id+"F0.wireOp",EDGE,"E0.bottom"),subQ0]}),-1.0]])],"derivedFrom":subQ0})])],"isStart":false});}
            var Q1;
            Q1=makeQuery(id+"F2.opExtrude","CAP_EDGE",EDGE,{"disambiguationData":[OSD([sQuery(id+"F0.wireOp",EDGE,"E0.bottom")])],"isStart":false});
            var Q2;
            {var subQ0=sQuery(id+"F0.wireOp",EDGE,"E0.right");Q2=makeQuery(id+"F2.opExtrude","CAP_EDGE",EDGE,{"disambiguationData":[OSD([subQ0]),TDD([makeQuery(id+"F0.imprint","IMPRINT",EDGE,{"disambiguationData":[TD([[makeQuery(id+"F0.imprint","INTERSECT",VERTEX,{"derivedFrom":[sQuery(id+"F0.wireOp",EDGE,"E0.bottom"),subQ0]}),-1.0]])],"derivedFrom":subQ0})])],"isStart":false});}
            var Q3;
            Q3=makeQuery(id+"F2.opExtrude","CAP_EDGE",EDGE,{"disambiguationData":[OSD([sQuery(id+"F0.wireOp",EDGE,"E5.top")])],"isStart":false});
            var Q4;
            Q4=makeQuery(id+"F2.opExtrude","CAP_EDGE",EDGE,{"disambiguationData":[OSD([sQuery(id+"F0.wireOp",EDGE,"E5.left")])],"isStart":false});
            var Q5;
            Q5=makeQuery(id+"F2.opExtrude","CAP_EDGE",EDGE,{"disambiguationData":[OSD([sQuery(id+"F0.wireOp",EDGE,"E4.top")])],"isStart":false});
            var Q6;
            Q6=makeQuery(id+"F2.opExtrude","CAP_EDGE",EDGE,{"disambiguationData":[OSD([sQuery(id+"F0.wireOp",EDGE,"E4.left")])],"isStart":false});
            var Q7;
            Q7=makeQuery(id+"F2.opExtrude","CAP_EDGE",EDGE,{"disambiguationData":[OSD([sQuery(id+"F0.wireOp",EDGE,"E4.bottom")])],"isStart":false});
            var Q8;
            {var subQ0=sQuery(id+"F0.wireOp",EDGE,"E0.left");Q8=makeQuery(id+"F2.opExtrude","CAP_EDGE",EDGE,{"disambiguationData":[OSD([subQ0]),TDD([makeQuery(id+"F0.imprint","IMPRINT",EDGE,{"disambiguationData":[TD([[makeQuery(id+"F0.imprint","INTERSECT",VERTEX,{"derivedFrom":[sQuery(id+"F0.wireOp",EDGE,"E0.top"),subQ0]}),1.0]])],"derivedFrom":subQ0})])],"isStart":false});}
            var Q9;
            Q9=makeQuery(id+"F2.opExtrude","CAP_EDGE",EDGE,{"disambiguationData":[OSD([sQuery(id+"F0.wireOp",EDGE,"E0.top")])],"isStart":false});
            var Q10;
            {var subQ0=sQuery(id+"F0.wireOp",EDGE,"E0.right");Q10=makeQuery(id+"F2.opExtrude","CAP_EDGE",EDGE,{"disambiguationData":[OSD([subQ0]),TDD([makeQuery(id+"F0.imprint","IMPRINT",EDGE,{"disambiguationData":[TD([[makeQuery(id+"F0.imprint","INTERSECT",VERTEX,{"derivedFrom":[sQuery(id+"F0.wireOp",EDGE,"E0.top"),subQ0]}),1.0]])],"derivedFrom":subQ0})])],"isStart":false});}
            var Q11;
            Q11=makeQuery(id+"F2.opExtrude","CAP_EDGE",EDGE,{"disambiguationData":[OSD([sQuery(id+"F0.wireOp",EDGE,"E5.bottom")])],"isStart":false});
            var Q12;
            Q12=makeQuery(id+"F2.opExtrude","SWEPT_EDGE",EDGE,{"disambiguationData":[OSD([sQuery(id+"F0.wireOp",EDGE,"E0.bottom"),sQuery(id+"F0.wireOp",EDGE,"E0.right")])]});
            var Q13;
            Q13=makeQuery(id+"F2.opExtrude","SWEPT_EDGE",EDGE,{"disambiguationData":[OSD([sQuery(id+"F0.wireOp",EDGE,"E0.bottom"),sQuery(id+"F0.wireOp",EDGE,"E0.left")])]});
            var Q14;
            Q14=makeQuery(id+"F2.opExtrude","SWEPT_EDGE",EDGE,{"disambiguationData":[OSD([sQuery(id+"F0.wireOp",EDGE,"E0.top"),sQuery(id+"F0.wireOp",EDGE,"E0.left")])]});
            var Q15;
            Q15=makeQuery(id+"F2.opExtrude","SWEPT_EDGE",EDGE,{"disambiguationData":[OSD([sQuery(id+"F0.wireOp",EDGE,"E0.top"),sQuery(id+"F0.wireOp",EDGE,"E0.right")])]});
            fillet(context, id + "F5", {"entities" : qUnion([Q0, Q1, Q2, Q3, Q4, Q5, Q6, Q7, Q8, Q9, Q10, Q11, Q12, Q13, Q14, Q15]), "radius" : 3.17 * mm, "tangentPropagation" : true, "allowEdgeOverflow" : false});
        }
        {
            var Q0;
            {var subQ0=sQuery(id+"F0.wireOp",EDGE,"E5.right");var subQ1=sQuery(id+"F0.wireOp",EDGE,"E4.right");var subQ2=sQuery(id+"F0.wireOp",EDGE,"E1.right");var subQ3=sQuery(id+"F0.wireOp",EDGE,"E1.left");var subQ4=sQuery(id+"F0.wireOp",EDGE,"E1.top");var subQ5=sQuery(id+"F0.wireOp",EDGE,"E1.bottom");Q0=makeQuery(id+"F2.boolean.opBoolean","MERGE",FACE,{"derivedFrom":[makeQuery(id+"F1.opExtrude","CAP_FACE",FACE,{"disambiguationData":[OSD([subQ5,subQ4,subQ3,subQ2,subQ1,subQ0])],"isStart":true}),makeQuery(id+"F2.opExtrude","CAP_FACE",FACE,{"disambiguationData":[OSD([sQuery(id+"F0.wireOp",EDGE,"E0.bottom"),sQuery(id+"F0.wireOp",EDGE,"E0.top"),sQuery(id+"F0.wireOp",EDGE,"E0.left"),sQuery(id+"F0.wireOp",EDGE,"E0.right"),subQ5,subQ4,subQ3,subQ2,sQuery(id+"F0.wireOp",EDGE,"E4.bottom"),sQuery(id+"F0.wireOp",EDGE,"E4.top"),sQuery(id+"F0.wireOp",EDGE,"E4.left"),subQ1,sQuery(id+"F0.wireOp",EDGE,"E5.bottom"),sQuery(id+"F0.wireOp",EDGE,"E5.top"),sQuery(id+"F0.wireOp",EDGE,"E5.left"),subQ0])],"isStart":true})]});}
            var sketch = newSketch(context, id + "F6", { "sketchPlane" : qUnion([Q0])});
            skLineSegment(sketch, "E8.bottom", {"start": v(-69.85, -25.14) * mm, "end": v(-63.5, -25.14) * mm});
            skLineSegment(sketch, "E8.top", {"start": v(-69.85, 25.66) * mm, "end": v(-63.5, 25.66) * mm});
            skLineSegment(sketch, "E8.left", {"start": v(-69.85, -25.14) * mm, "end": v(-69.85, 25.66) * mm});
            skLineSegment(sketch, "E8.right", {"start": v(-63.5, -25.14) * mm, "end": v(-63.5, 25.66) * mm});
            skLineSegment(sketch, "E9.bottom", {"start": v(69.85, -25.14) * mm, "end": v(63.5, -25.14) * mm});
            skLineSegment(sketch, "E9.top", {"start": v(69.85, 25.66) * mm, "end": v(63.5, 25.66) * mm});
            skLineSegment(sketch, "E9.left", {"start": v(69.85, -25.14) * mm, "end": v(69.85, 25.66) * mm});
            skLineSegment(sketch, "E9.right", {"start": v(63.5, -25.14) * mm, "end": v(63.5, 25.66) * mm});
            skSolve(sketch);
        }
        {
            var Q0;
            Q0=makeQuery(id+"F6.imprint","IMPRINT",FACE,{"disambiguationData":[TD([[makeQuery(id+"F6.imprint","IMPRINT",EDGE,{"derivedFrom":sQuery(id+"F6.wireOp",EDGE,"E8.bottom")}),1.0]])]});
            var Q1;
            Q1=makeQuery(id+"F6.imprint","IMPRINT",FACE,{"disambiguationData":[TD([[makeQuery(id+"F6.imprint","IMPRINT",EDGE,{"derivedFrom":sQuery(id+"F6.wireOp",EDGE,"E9.bottom")}),-1.0]])]});
            extrude(context, id + "F7", {"entities" : qUnion([Q0, Q1]), "operationType" : NewBodyOperationType.REMOVE, "oppositeDirection" : true, "depth" : 9.52 * mm, "offsetDistance" : 25.4 * mm});
        }
        {
            var Q0;
            Q0=makeQuery(id+"F2.opExtrude","SWEPT_FACE",FACE,{"disambiguationData":[OSD([sQuery(id+"F0.wireOp",EDGE,"E0.bottom")])]});
            var sketch = newSketch(context, id + "F8", { "sketchPlane" : qUnion([Q0])});
            skText(sketch, "E10", { "text": "1/4 x 1", "fontName": "OpenSans-Regular.ttf"});
            const initialGuessF8  = {"E10": [-0.05552, 0.00362, 1, 0, 0.009]};
            skSetInitialGuess(sketch, initialGuessF8);
            skSolve(sketch);
        }
        {
            var Q0;
            Q0 = qSketchRegion(id + "F8", true);
            extrude(context, id + "F9", {"entities" : qUnion([Q0]), "operationType" : NewBodyOperationType.REMOVE, "oppositeDirection" : true, "depth" : 3.17 * mm, "offsetDistance" : 25.4 * mm});
        }
    });
